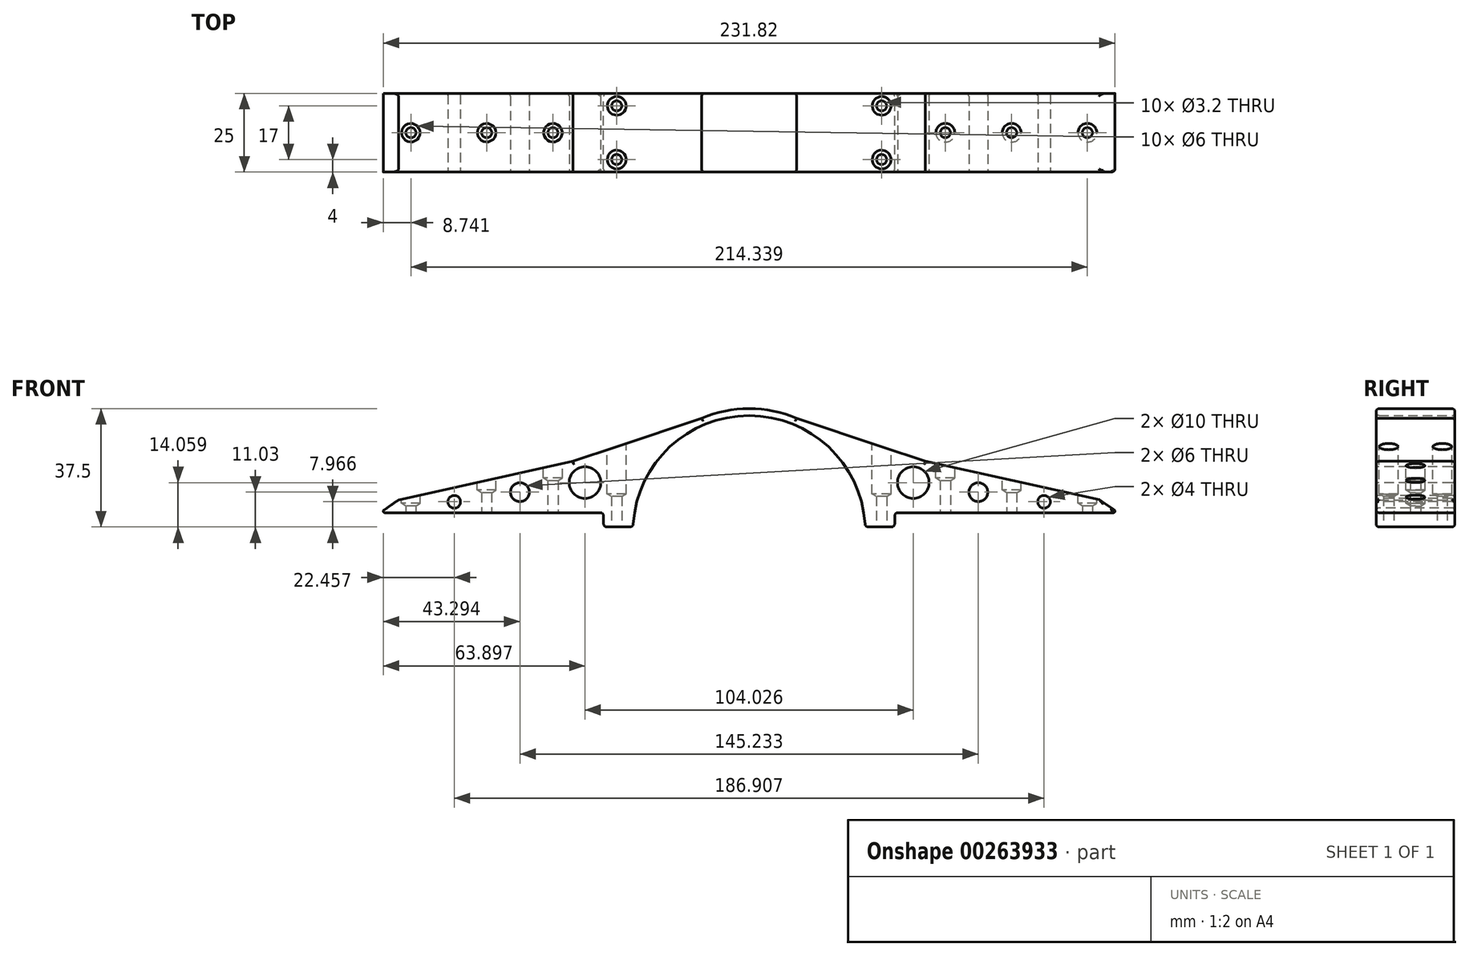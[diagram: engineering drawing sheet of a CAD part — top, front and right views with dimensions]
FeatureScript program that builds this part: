
annotation { "Feature Type Name" : "Feature", "Feature Type Description" : "" }
export const myFeature = defineFeature(function(context is Context, id is Id, definition is map)
    precondition{}
    {
        {
            var Q0;
            Q0=qCreatedBy(makeId("Front.planeOp"),FACE);
            var sketch = newSketch(context, id + "F0", { "sketchPlane" : qUnion([Q0])});
            skLineSegment(sketch, "E0", {"start": v(-117.03, 6) * mm, "end": v(-46.11, 6) * mm});
            skLineSegment(sketch, "E1", {"start": v(117.03, 6) * mm, "end": v(111.07, 10.06) * mm});
            skLineSegment(sketch, "E2", {"start": v(111.07, 10.06) * mm, "end": v(55.86, 22.32) * mm});
            skLineSegment(sketch, "E3", {"start": v(55.86, 22.32) * mm, "end": v(15, 36) * mm});
            skArc(sketch, "E4", {"start": v(15, 36) * mm, "mid": v(0, 39) * mm, "end": v(-15, 36) * mm});
            skPoint(sketch, "E5.start.orphan", {"position": v(39, 0) * mm});
            skLineSegment(sketch, "E6", {"start": v(36.71, 1.5) * mm, "end": v(46.11, 1.5) * mm});
            skLineSegment(sketch, "E7", {"start": v(46.11, 1.5) * mm, "end": v(46.11, 6) * mm});
            skLineSegment(sketch, "E8", {"start": v(15, 36) * mm, "end": v(15, 36) * mm});
            skArc(sketch, "E9", {"start": v(36.77, 1.5) * mm, "mid": v(0, 36.8) * mm, "end": v(-36.77, 1.5) * mm});
            skPoint(sketch, "E10.start.orphan", {"position": v(36.8, 0) * mm});
            skLineSegment(sketch, "E11", {"start": v(46.11, 6) * mm, "end": v(117.03, 6) * mm});
            skLineSegment(sketch, "E12.MirrorCS", {"start": v(-46.11, 1.5) * mm, "end": v(-46.11, 6) * mm});
            skLineSegment(sketch, "E13.MirrorCS", {"start": v(-36.71, 1.5) * mm, "end": v(-46.11, 1.5) * mm});
            skLineSegment(sketch, "E14.MirrorCS", {"start": v(-55.86, 22.32) * mm, "end": v(-15, 36) * mm});
            skLineSegment(sketch, "E15.MirrorCS", {"start": v(-111.07, 10.06) * mm, "end": v(-55.86, 22.32) * mm});
            skLineSegment(sketch, "E16.MirrorCS", {"start": v(-117.03, 6) * mm, "end": v(-111.07, 10.06) * mm});
            skSolve(sketch);
        }
        {
            var Q0;
            Q0 = qSketchRegion(id + "F0", true);
            extrude(context, id + "F1", {"entities" : qUnion([Q0]), "depth" : 25 * mm});
        }
        {
            var Q0;
            Q0=makeQuery(id+"F1.opExtrude","SWEPT_FACE",FACE,{"disambiguationData":[OSD([sQuery(id+"F0.wireOp",EDGE,"E6")])]});
            var sketch = newSketch(context, id + "F2", { "sketchPlane" : qUnion([Q0])});
            skLineSegment(sketch, "E17.0", {"start": v(36.77, 25) * mm, "end": v(36.77, 0) * mm});
            skPoint(sketch, "E18.0", {"position": v(41.44, 25) * mm});
            skLineSegment(sketch, "E19.0", {"start": v(46.11, 25) * mm, "end": v(46.11, 0) * mm});
            skPoint(sketch, "E20.0", {"position": v(41.44, 0) * mm});
            skLineSegment(sketch, "E21.0", {"start": v(36.77, 0) * mm, "end": v(46.11, 0) * mm});
            skLineSegment(sketch, "E22.0", {"start": v(36.77, 25) * mm, "end": v(46.11, 25) * mm});
            skLineSegment(sketch, "E23", {"start": v(41.97, 30.62) * mm, "end": v(41.97, -11.26) * mm, "construction": true});
            skCircle(sketch, "E24", {"center": v(41.97, 21) * mm, "radius": 1.75 * mm});
            skCircle(sketch, "E25", {"center": v(41.97, 4) * mm, "radius": 1.75 * mm});
            skCircle(sketch, "E26.MirrorC", {"center": v(-41.97, 21) * mm, "radius": 1.75 * mm});
            skCircle(sketch, "E27.MirrorC", {"center": v(-41.97, 4) * mm, "radius": 1.75 * mm});
            skSolve(sketch);
        }
        {
            var Q0;
            Q0=sQuery(id+"F2.wireOp",VERTEX,"E24.center");
            var Q1;
            Q1=sQuery(id+"F2.wireOp",VERTEX,"E25.center");
            var Q2;
            Q2=sQuery(id+"F2.wireOp",VERTEX,"E26.MirrorC.center");
            var Q3;
            Q3=sQuery(id+"F2.wireOp",VERTEX,"E27.MirrorC.center");
            var Q4;
            Q4=makeQuery(id+"F1.opExtrude","SWEPT_BODY",BODY,{"disambiguationData":[OSD([sQuery(id+"F0.wireOp",EDGE,"E0"),sQuery(id+"F0.wireOp",EDGE,"E1"),sQuery(id+"F0.wireOp",EDGE,"E2"),sQuery(id+"F0.wireOp",EDGE,"E3"),sQuery(id+"F0.wireOp",EDGE,"E4"),sQuery(id+"F0.wireOp",EDGE,"E6"),sQuery(id+"F0.wireOp",EDGE,"E7"),sQuery(id+"F0.wireOp",EDGE,"E9"),sQuery(id+"F0.wireOp",EDGE,"E11"),sQuery(id+"F0.wireOp",EDGE,"E12.MirrorCS"),sQuery(id+"F0.wireOp",EDGE,"E13.MirrorCS"),sQuery(id+"F0.wireOp",EDGE,"E14.MirrorCS"),sQuery(id+"F0.wireOp",EDGE,"E15.MirrorCS"),sQuery(id+"F0.wireOp",EDGE,"E16.MirrorCS")])]});
            hole(context, id + "F3", {"style" : HoleStyle.SIMPLE, "endStyle" : HoleEndStyle.THROUGH, "standardTappedOrClearance" : lookupTablePath({ "standard" : "ISO", "engagement" : "75%", "pitch" : "0.75 mm", "size" : "M4", "type" : "Tapped" }), "standardBlindInLast" : lookupTablePath({ "standard" : "ISO", "engagement" : "75%", "pitch" : "0.75 mm", "size" : "M4", "type" : "Tapped" }), "holeDiameter" : 3.2 * mm, "showTappedDepth" : true, "tappedDepth" : 12 * mm, "tapClearance" : 3, "locations" : qUnion([Q0, Q1, Q2, Q3]), "scope" : qUnion([Q4])});
        }
        {
            var Q0;
            Q0=makeQuery(id+"F1.opExtrude","SWEPT_FACE",FACE,{"disambiguationData":[OSD([sQuery(id+"F0.wireOp",EDGE,"E11")])]});
            var sketch = newSketch(context, id + "F4", { "sketchPlane" : qUnion([Q0])});
            skLineSegment(sketch, "E28.0", {"start": v(36.77, 25) * mm, "end": v(36.77, 0) * mm});
            skLineSegment(sketch, "E29.0", {"start": v(36.77, 25) * mm, "end": v(46.11, 25) * mm});
            skLineSegment(sketch, "E30.0", {"start": v(36.77, 0) * mm, "end": v(46.11, 0) * mm});
            skLineSegment(sketch, "E31.0", {"start": v(46.11, 25) * mm, "end": v(46.11, 0) * mm});
            skLineSegment(sketch, "E32.0", {"start": v(46.11, 25) * mm, "end": v(117.03, 25) * mm});
            skLineSegment(sketch, "E33.0", {"start": v(46.11, 0) * mm, "end": v(117.03, 0) * mm});
            skLineSegment(sketch, "E34", {"start": v(-152.17, 12.5) * mm, "end": v(189.53, 12.5) * mm, "construction": true});
            skLineSegment(sketch, "E35.0", {"start": v(-117.03, 25) * mm, "end": v(-46.11, 25) * mm});
            skLineSegment(sketch, "E36.0", {"start": v(-117.03, 0) * mm, "end": v(-46.11, 0) * mm});
            skCircle(sketch, "E37", {"center": v(62.17, 12.5) * mm, "radius": 1.5 * mm});
            skCircle(sketch, "E38", {"center": v(83.17, 12.5) * mm, "radius": 1.5 * mm});
            skCircle(sketch, "E39", {"center": v(107.17, 12.5) * mm, "radius": 1.5 * mm});
            skLineSegment(sketch, "E40", {"start": v(47.17, 31.58) * mm, "end": v(47.17, -3.17) * mm, "construction": true});
            skCircle(sketch, "E41.MirrorC", {"center": v(-62.17, 12.5) * mm, "radius": 1.5 * mm});
            skCircle(sketch, "E42.MirrorC", {"center": v(-83.17, 12.5) * mm, "radius": 1.5 * mm});
            skCircle(sketch, "E43.MirrorC", {"center": v(-107.17, 12.5) * mm, "radius": 1.5 * mm});
            skSolve(sketch);
        }
        {
            var Q0;
            Q0=sQuery(id+"F4.wireOp",VERTEX,"E39.center");
            var Q1;
            Q1=sQuery(id+"F4.wireOp",VERTEX,"E38.center");
            var Q2;
            Q2=sQuery(id+"F4.wireOp",VERTEX,"E37.center");
            var Q3;
            Q3=sQuery(id+"F4.wireOp",VERTEX,"E41.MirrorC.center");
            var Q4;
            Q4=sQuery(id+"F4.wireOp",VERTEX,"E42.MirrorC.center");
            var Q5;
            Q5=sQuery(id+"F4.wireOp",VERTEX,"E43.MirrorC.center");
            var Q6;
            Q6=makeQuery(id+"F1.opExtrude","SWEPT_BODY",BODY,{"disambiguationData":[OSD([sQuery(id+"F0.wireOp",EDGE,"E0"),sQuery(id+"F0.wireOp",EDGE,"E1"),sQuery(id+"F0.wireOp",EDGE,"E2"),sQuery(id+"F0.wireOp",EDGE,"E3"),sQuery(id+"F0.wireOp",EDGE,"E4"),sQuery(id+"F0.wireOp",EDGE,"E6"),sQuery(id+"F0.wireOp",EDGE,"E7"),sQuery(id+"F0.wireOp",EDGE,"E9"),sQuery(id+"F0.wireOp",EDGE,"E11"),sQuery(id+"F0.wireOp",EDGE,"E12.MirrorCS"),sQuery(id+"F0.wireOp",EDGE,"E13.MirrorCS"),sQuery(id+"F0.wireOp",EDGE,"E14.MirrorCS"),sQuery(id+"F0.wireOp",EDGE,"E15.MirrorCS"),sQuery(id+"F0.wireOp",EDGE,"E16.MirrorCS")])]});
            hole(context, id + "F5", {"style" : HoleStyle.SIMPLE, "endStyle" : HoleEndStyle.THROUGH, "standardTappedOrClearance" : lookupTablePath({ "standard" : "ISO", "engagement" : "75%", "pitch" : "0.75 mm", "size" : "M4", "type" : "Tapped" }), "standardBlindInLast" : lookupTablePath({ "standard" : "ISO", "engagement" : "75%", "pitch" : "0.75 mm", "size" : "M4", "type" : "Tapped" }), "holeDiameter" : 3.2 * mm, "showTappedDepth" : true, "tappedDepth" : 12 * mm, "tapClearance" : 3, "locations" : qUnion([Q0, Q1, Q2, Q3, Q4, Q5]), "scope" : qUnion([Q6])});
        }
        {
            var Q0;
            Q0=qCreatedBy(makeId("Top.planeOp"),FACE);
            cPlane(context, id + "F6", {"entities" : qUnion([Q0]), "cplaneType" : CPlaneType.OFFSET, "offset" : 28 * mm, "width" : 150 * mm, "height" : 150 * mm});
        }
        {
            var Q0;
            Q0=qCreatedBy(id+"F6.planeOp",FACE);
            var sketch = newSketch(context, id + "F7", { "sketchPlane" : qUnion([Q0])});
            skCircle(sketch, "E44.0", {"center": v(41.97, -4) * mm, "radius": 1.6 * mm, "construction": true});
            skCircle(sketch, "E45.0", {"center": v(41.97, -21) * mm, "radius": 1.6 * mm, "construction": true});
            skCircle(sketch, "E46.0", {"center": v(62.17, -12.5) * mm, "radius": 1.6 * mm});
            skCircle(sketch, "E47.0", {"center": v(83.17, -12.5) * mm, "radius": 1.6 * mm});
            skCircle(sketch, "E48.0", {"center": v(107.17, -12.5) * mm, "radius": 1.6 * mm});
            skCircle(sketch, "E49.0", {"center": v(-41.97, -4) * mm, "radius": 1.6 * mm, "construction": true});
            skCircle(sketch, "E50.0", {"center": v(-41.97, -21) * mm, "radius": 1.6 * mm, "construction": true});
            skCircle(sketch, "E51.0", {"center": v(-62.17, -12.5) * mm, "radius": 1.6 * mm});
            skCircle(sketch, "E52.0", {"center": v(-83.17, -12.5) * mm, "radius": 1.2 * mm});
            skCircle(sketch, "E53.0", {"center": v(-107.17, -12.5) * mm, "radius": 1.2 * mm});
            skCircle(sketch, "E54", {"center": v(41.97, -4) * mm, "radius": 2 * mm});
            skCircle(sketch, "E55", {"center": v(41.97, -21) * mm, "radius": 2 * mm});
            skCircle(sketch, "E56.MirrorC", {"center": v(-41.97, -4) * mm, "radius": 2 * mm});
            skCircle(sketch, "E57.MirrorC", {"center": v(-41.97, -21) * mm, "radius": 2 * mm});
            skSolve(sketch);
        }
        {
            var Q0;
            Q0=sQuery(id+"F7.wireOp",VERTEX,"E44.0.center");
            var Q1;
            Q1=sQuery(id+"F7.wireOp",VERTEX,"E45.0.center");
            var Q2;
            Q2=sQuery(id+"F7.wireOp",VERTEX,"E50.0.center");
            var Q3;
            Q3=sQuery(id+"F7.wireOp",VERTEX,"E49.0.center");
            var Q4;
            Q4=makeQuery(id+"F1.opExtrude","SWEPT_BODY",BODY,{"disambiguationData":[OSD([sQuery(id+"F0.wireOp",EDGE,"E0"),sQuery(id+"F0.wireOp",EDGE,"E1"),sQuery(id+"F0.wireOp",EDGE,"E2"),sQuery(id+"F0.wireOp",EDGE,"E3"),sQuery(id+"F0.wireOp",EDGE,"E4"),sQuery(id+"F0.wireOp",EDGE,"E6"),sQuery(id+"F0.wireOp",EDGE,"E7"),sQuery(id+"F0.wireOp",EDGE,"E9"),sQuery(id+"F0.wireOp",EDGE,"E11"),sQuery(id+"F0.wireOp",EDGE,"E12.MirrorCS"),sQuery(id+"F0.wireOp",EDGE,"E13.MirrorCS"),sQuery(id+"F0.wireOp",EDGE,"E14.MirrorCS"),sQuery(id+"F0.wireOp",EDGE,"E15.MirrorCS"),sQuery(id+"F0.wireOp",EDGE,"E16.MirrorCS")])]});
            hole(context, id + "F8", {"style" : HoleStyle.SIMPLE, "endStyle" : HoleEndStyle.BLIND, "holeDiameter" : 6 * mm, "holeDepth" : 16 * mm, "tappedDepth" : 12 * mm, "tapClearance" : 3, "startFromSketch" : true, "locations" : qUnion([Q0, Q1, Q2, Q3]), "scope" : qUnion([Q4])});
        }
        {
            var Q0;
            Q0=sQuery(id+"F7.wireOp",VERTEX,"E46.0.center");
            var Q1;
            Q1=sQuery(id+"F7.wireOp",VERTEX,"E51.0.center");
            var Q2;
            Q2=makeQuery(id+"F1.opExtrude","SWEPT_BODY",BODY,{"disambiguationData":[OSD([sQuery(id+"F0.wireOp",EDGE,"E0"),sQuery(id+"F0.wireOp",EDGE,"E1"),sQuery(id+"F0.wireOp",EDGE,"E2"),sQuery(id+"F0.wireOp",EDGE,"E3"),sQuery(id+"F0.wireOp",EDGE,"E4"),sQuery(id+"F0.wireOp",EDGE,"E6"),sQuery(id+"F0.wireOp",EDGE,"E7"),sQuery(id+"F0.wireOp",EDGE,"E9"),sQuery(id+"F0.wireOp",EDGE,"E11"),sQuery(id+"F0.wireOp",EDGE,"E12.MirrorCS"),sQuery(id+"F0.wireOp",EDGE,"E13.MirrorCS"),sQuery(id+"F0.wireOp",EDGE,"E14.MirrorCS"),sQuery(id+"F0.wireOp",EDGE,"E15.MirrorCS"),sQuery(id+"F0.wireOp",EDGE,"E16.MirrorCS")])]});
            hole(context, id + "F9", {"style" : HoleStyle.SIMPLE, "endStyle" : HoleEndStyle.BLIND, "holeDiameter" : 6 * mm, "holeDepth" : 11 * mm, "tappedDepth" : 8 * mm, "tapClearance" : 3, "startFromSketch" : true, "locations" : qUnion([Q0, Q1]), "scope" : qUnion([Q2])});
        }
        {
            var Q0;
            Q0=sQuery(id+"F7.wireOp",VERTEX,"E52.0.center");
            var Q1;
            Q1=sQuery(id+"F7.wireOp",VERTEX,"E47.0.center");
            var Q2;
            Q2=makeQuery(id+"F1.opExtrude","SWEPT_BODY",BODY,{"disambiguationData":[OSD([sQuery(id+"F0.wireOp",EDGE,"E0"),sQuery(id+"F0.wireOp",EDGE,"E1"),sQuery(id+"F0.wireOp",EDGE,"E2"),sQuery(id+"F0.wireOp",EDGE,"E3"),sQuery(id+"F0.wireOp",EDGE,"E4"),sQuery(id+"F0.wireOp",EDGE,"E6"),sQuery(id+"F0.wireOp",EDGE,"E7"),sQuery(id+"F0.wireOp",EDGE,"E9"),sQuery(id+"F0.wireOp",EDGE,"E11"),sQuery(id+"F0.wireOp",EDGE,"E12.MirrorCS"),sQuery(id+"F0.wireOp",EDGE,"E13.MirrorCS"),sQuery(id+"F0.wireOp",EDGE,"E14.MirrorCS"),sQuery(id+"F0.wireOp",EDGE,"E15.MirrorCS"),sQuery(id+"F0.wireOp",EDGE,"E16.MirrorCS")])]});
            hole(context, id + "F10", {"style" : HoleStyle.SIMPLE, "endStyle" : HoleEndStyle.BLIND, "holeDiameter" : 6 * mm, "holeDepth" : 14.85 * mm, "tappedDepth" : 11.1 * mm, "tapClearance" : 3, "startFromSketch" : true, "locations" : qUnion([Q0, Q1]), "scope" : qUnion([Q2])});
        }
        {
            var Q0;
            Q0=sQuery(id+"F7.wireOp",VERTEX,"E53.0.center");
            var Q1;
            Q1=sQuery(id+"F7.wireOp",VERTEX,"E48.0.center");
            var Q2;
            Q2=makeQuery(id+"F1.opExtrude","SWEPT_BODY",BODY,{"disambiguationData":[OSD([sQuery(id+"F0.wireOp",EDGE,"E0"),sQuery(id+"F0.wireOp",EDGE,"E1"),sQuery(id+"F0.wireOp",EDGE,"E2"),sQuery(id+"F0.wireOp",EDGE,"E3"),sQuery(id+"F0.wireOp",EDGE,"E4"),sQuery(id+"F0.wireOp",EDGE,"E6"),sQuery(id+"F0.wireOp",EDGE,"E7"),sQuery(id+"F0.wireOp",EDGE,"E9"),sQuery(id+"F0.wireOp",EDGE,"E11"),sQuery(id+"F0.wireOp",EDGE,"E12.MirrorCS"),sQuery(id+"F0.wireOp",EDGE,"E13.MirrorCS"),sQuery(id+"F0.wireOp",EDGE,"E14.MirrorCS"),sQuery(id+"F0.wireOp",EDGE,"E15.MirrorCS"),sQuery(id+"F0.wireOp",EDGE,"E16.MirrorCS")])]});
            hole(context, id + "F11", {"style" : HoleStyle.SIMPLE, "endStyle" : HoleEndStyle.BLIND, "holeDiameter" : 6 * mm, "holeDepth" : 19 * mm, "tappedDepth" : 16.1 * mm, "tapClearance" : 3, "startFromSketch" : true, "locations" : qUnion([Q0, Q1]), "scope" : qUnion([Q2])});
        }
        {
            var Q0;
            Q0=makeQuery(id+"F1.opExtrude","CAP_FACE",FACE,{"disambiguationData":[OSD([sQuery(id+"F0.wireOp",EDGE,"E0"),sQuery(id+"F0.wireOp",EDGE,"E1"),sQuery(id+"F0.wireOp",EDGE,"E2"),sQuery(id+"F0.wireOp",EDGE,"E3"),sQuery(id+"F0.wireOp",EDGE,"E4"),sQuery(id+"F0.wireOp",EDGE,"E6"),sQuery(id+"F0.wireOp",EDGE,"E7"),sQuery(id+"F0.wireOp",EDGE,"E9"),sQuery(id+"F0.wireOp",EDGE,"E11"),sQuery(id+"F0.wireOp",EDGE,"E12.MirrorCS"),sQuery(id+"F0.wireOp",EDGE,"E13.MirrorCS"),sQuery(id+"F0.wireOp",EDGE,"E14.MirrorCS"),sQuery(id+"F0.wireOp",EDGE,"E15.MirrorCS"),sQuery(id+"F0.wireOp",EDGE,"E16.MirrorCS")])],"isStart":false});
            var sketch = newSketch(context, id + "F12", { "sketchPlane" : qUnion([Q0])});
            skCircle(sketch, "E58", {"center": v(-52.01, 15.56) * mm, "radius": 5 * mm});
            skLineSegment(sketch, "E59", {"start": v(-62.12, 28.15) * mm, "end": v(-62.12, 0) * mm, "construction": true});
            skLineSegment(sketch, "E60", {"start": v(-41.91, 28) * mm, "end": v(-41.91, -0.66) * mm, "construction": true});
            skLineSegment(sketch, "E61", {"start": v(-83.2, 28.15) * mm, "end": v(-83.2, -0.74) * mm, "construction": true});
            skLineSegment(sketch, "E62", {"start": v(-83.31, -0.74) * mm, "end": v(-83.82, -0.74) * mm, "construction": true});
            skLineSegment(sketch, "E63", {"start": v(-107.05, 28) * mm, "end": v(-107.05, 0) * mm, "construction": true});
            skCircle(sketch, "E64", {"center": v(-72.62, 12.53) * mm, "radius": 3 * mm});
            skLineSegment(sketch, "E65", {"start": v(-117.03, 6) * mm, "end": v(-31.8, 18.53) * mm, "construction": true});
            skCircle(sketch, "E66", {"center": v(-93.45, 9.47) * mm, "radius": 2 * mm});
            skCircle(sketch, "E67.MirrorC", {"center": v(52.01, 15.56) * mm, "radius": 5 * mm});
            skCircle(sketch, "E68.MirrorC", {"center": v(72.62, 12.53) * mm, "radius": 3 * mm});
            skCircle(sketch, "E69.MirrorC", {"center": v(93.45, 9.47) * mm, "radius": 2 * mm});
            skSolve(sketch);
        }
        {
            var Q0;
            Q0 = qSketchRegion(id + "F12", true);
            extrude(context, id + "F13", {"entities" : qUnion([Q0]), "operationType" : NewBodyOperationType.REMOVE, "endBound" : BoundingType.THROUGH_ALL, "oppositeDirection" : true, "depth" : 25 * mm});
        }
        {
            var Q0;
            Q0=makeQuery(id+"F1.opExtrude","SWEPT_EDGE",EDGE,{"disambiguationData":[OSD([sQuery(id+"F0.wireOp",EDGE,"E9"),sQuery(id+"F0.wireOp",EDGE,"E13.MirrorCS")])]});
            var Q1;
            Q1=makeQuery(id+"F1.opExtrude","SWEPT_EDGE",EDGE,{"disambiguationData":[OSD([sQuery(id+"F0.wireOp",EDGE,"E6"),sQuery(id+"F0.wireOp",EDGE,"E9")])]});
            var Q2;
            Q2=makeQuery(id+"F1.opExtrude","SWEPT_EDGE",EDGE,{"disambiguationData":[OSD([sQuery(id+"F0.wireOp",EDGE,"E7"),sQuery(id+"F0.wireOp",EDGE,"E11")])]});
            var Q3;
            Q3=makeQuery(id+"F1.opExtrude","SWEPT_EDGE",EDGE,{"disambiguationData":[OSD([sQuery(id+"F0.wireOp",EDGE,"E6"),sQuery(id+"F0.wireOp",EDGE,"E7")])]});
            var Q4;
            Q4=makeQuery(id+"F1.opExtrude","SWEPT_EDGE",EDGE,{"disambiguationData":[OSD([sQuery(id+"F0.wireOp",EDGE,"E12.MirrorCS"),sQuery(id+"F0.wireOp",EDGE,"E13.MirrorCS")])]});
            var Q5;
            Q5=makeQuery(id+"F1.opExtrude","SWEPT_EDGE",EDGE,{"disambiguationData":[OSD([sQuery(id+"F0.wireOp",EDGE,"E0"),sQuery(id+"F0.wireOp",EDGE,"E12.MirrorCS")])]});
            var Q6;
            Q6=makeQuery(id+"F1.opExtrude","CAP_EDGE",EDGE,{"disambiguationData":[OSD([sQuery(id+"F0.wireOp",EDGE,"E12.MirrorCS")])],"isStart":true});
            var Q7;
            Q7=makeQuery(id+"F1.opExtrude","CAP_EDGE",EDGE,{"disambiguationData":[OSD([sQuery(id+"F0.wireOp",EDGE,"E13.MirrorCS")])],"isStart":true});
            var Q8;
            Q8=makeQuery(id+"F1.opExtrude","CAP_EDGE",EDGE,{"disambiguationData":[OSD([sQuery(id+"F0.wireOp",EDGE,"E6")])],"isStart":true});
            var Q9;
            Q9=makeQuery(id+"F1.opExtrude","CAP_EDGE",EDGE,{"disambiguationData":[OSD([sQuery(id+"F0.wireOp",EDGE,"E7")])],"isStart":true});
            var Q10;
            Q10=makeQuery(id+"F1.opExtrude","CAP_EDGE",EDGE,{"disambiguationData":[OSD([sQuery(id+"F0.wireOp",EDGE,"E12.MirrorCS")])],"isStart":false});
            var Q11;
            Q11=makeQuery(id+"F1.opExtrude","CAP_EDGE",EDGE,{"disambiguationData":[OSD([sQuery(id+"F0.wireOp",EDGE,"E13.MirrorCS")])],"isStart":false});
            var Q12;
            Q12=makeQuery(id+"F1.opExtrude","CAP_EDGE",EDGE,{"disambiguationData":[OSD([sQuery(id+"F0.wireOp",EDGE,"E6")])],"isStart":false});
            var Q13;
            Q13=makeQuery(id+"F1.opExtrude","CAP_EDGE",EDGE,{"disambiguationData":[OSD([sQuery(id+"F0.wireOp",EDGE,"E7")])],"isStart":false});
            var Q14;
            Q14=makeQuery(id+"F1.opExtrude","CAP_EDGE",EDGE,{"disambiguationData":[OSD([sQuery(id+"F0.wireOp",EDGE,"E11")])],"isStart":false});
            var Q15;
            Q15=makeQuery(id+"F1.opExtrude","CAP_EDGE",EDGE,{"disambiguationData":[OSD([sQuery(id+"F0.wireOp",EDGE,"E9")])],"isStart":false});
            var Q16;
            Q16=makeQuery(id+"F1.opExtrude","CAP_EDGE",EDGE,{"disambiguationData":[OSD([sQuery(id+"F0.wireOp",EDGE,"E9")])],"isStart":true});
            fillet(context, id + "F14", {"entities" : qUnion([Q0, Q1, Q2, Q3, Q4, Q5, Q6, Q7, Q8, Q9, Q10, Q11, Q12, Q13, Q14, Q15, Q16]), "radius" : 1 * mm, "tangentPropagation" : true, "allowEdgeOverflow" : false});
        }
        {
            var Q0;
            Q0=makeQuery(id+"F1.opExtrude","SWEPT_EDGE",EDGE,{"disambiguationData":[OSD([sQuery(id+"F0.wireOp",EDGE,"E0"),sQuery(id+"F0.wireOp",EDGE,"E16.MirrorCS")])]});
            var Q1;
            Q1=makeQuery(id+"F1.opExtrude","SWEPT_EDGE",EDGE,{"disambiguationData":[OSD([sQuery(id+"F0.wireOp",EDGE,"E1"),sQuery(id+"F0.wireOp",EDGE,"E11")])]});
            fillet(context, id + "F15", {"entities" : qUnion([Q0, Q1]), "radius" : .5 * mm, "tangentPropagation" : true, "allowEdgeOverflow" : false});
        }
        {
            var Q0;
            Q0=makeQuery(id+"F1.opExtrude","CAP_EDGE",EDGE,{"disambiguationData":[OSD([sQuery(id+"F0.wireOp",EDGE,"E15.MirrorCS")])],"isStart":false});
            var Q1;
            Q1=makeQuery(id+"F1.opExtrude","CAP_EDGE",EDGE,{"disambiguationData":[OSD([sQuery(id+"F0.wireOp",EDGE,"E14.MirrorCS")])],"isStart":false});
            var Q2;
            Q2=makeQuery(id+"F1.opExtrude","CAP_EDGE",EDGE,{"disambiguationData":[OSD([sQuery(id+"F0.wireOp",EDGE,"E4")])],"isStart":false});
            var Q3;
            Q3=makeQuery(id+"F1.opExtrude","CAP_EDGE",EDGE,{"disambiguationData":[OSD([sQuery(id+"F0.wireOp",EDGE,"E3")])],"isStart":false});
            var Q4;
            Q4=makeQuery(id+"F1.opExtrude","CAP_EDGE",EDGE,{"disambiguationData":[OSD([sQuery(id+"F0.wireOp",EDGE,"E2")])],"isStart":false});
            var Q5;
            Q5=makeQuery(id+"F1.opExtrude","CAP_EDGE",EDGE,{"disambiguationData":[OSD([sQuery(id+"F0.wireOp",EDGE,"E2")])],"isStart":true});
            var Q6;
            Q6=makeQuery(id+"F1.opExtrude","CAP_EDGE",EDGE,{"disambiguationData":[OSD([sQuery(id+"F0.wireOp",EDGE,"E3")])],"isStart":true});
            var Q7;
            Q7=makeQuery(id+"F1.opExtrude","CAP_EDGE",EDGE,{"disambiguationData":[OSD([sQuery(id+"F0.wireOp",EDGE,"E4")])],"isStart":true});
            var Q8;
            Q8=makeQuery(id+"F1.opExtrude","CAP_EDGE",EDGE,{"disambiguationData":[OSD([sQuery(id+"F0.wireOp",EDGE,"E14.MirrorCS")])],"isStart":true});
            var Q9;
            Q9=makeQuery(id+"F1.opExtrude","CAP_EDGE",EDGE,{"disambiguationData":[OSD([sQuery(id+"F0.wireOp",EDGE,"E15.MirrorCS")])],"isStart":true});
            var Q10;
            Q10=makeQuery(id+"F13.boolean.opBoolean","COPY",EDGE,{"derivedFrom":makeQuery(id+"F13.opExtrude","CAP_EDGE",EDGE,{"disambiguationData":[OSD([sQuery(id+"F12.wireOp",EDGE,"E64")])],"isStart":true})});
            var Q11;
            Q11=makeQuery(id+"F13.boolean.opBoolean","COPY",EDGE,{"derivedFrom":makeQuery(id+"F13.opExtrude","CAP_EDGE",EDGE,{"disambiguationData":[OSD([sQuery(id+"F12.wireOp",EDGE,"E58")])],"isStart":true})});
            var Q12;
            Q12=makeQuery(id+"F13.boolean.opBoolean","COPY",EDGE,{"derivedFrom":makeQuery(id+"F13.opExtrude","CAP_EDGE",EDGE,{"disambiguationData":[OSD([sQuery(id+"F12.wireOp",EDGE,"E67.MirrorC")])],"isStart":true})});
            var Q13;
            Q13=makeQuery(id+"F13.boolean.opBoolean","COPY",EDGE,{"derivedFrom":makeQuery(id+"F13.opExtrude","CAP_EDGE",EDGE,{"disambiguationData":[OSD([sQuery(id+"F12.wireOp",EDGE,"E68.MirrorC")])],"isStart":true})});
            var Q14;
            Q14=makeQuery(id+"F13.boolean.opBoolean","INTERSECT",EDGE,{"derivedFrom":[makeQuery(id+"F1.opExtrude","CAP_FACE",FACE,{"disambiguationData":[OSD([sQuery(id+"F0.wireOp",EDGE,"E0"),sQuery(id+"F0.wireOp",EDGE,"E1"),sQuery(id+"F0.wireOp",EDGE,"E2"),sQuery(id+"F0.wireOp",EDGE,"E3"),sQuery(id+"F0.wireOp",EDGE,"E4"),sQuery(id+"F0.wireOp",EDGE,"E6"),sQuery(id+"F0.wireOp",EDGE,"E7"),sQuery(id+"F0.wireOp",EDGE,"E9"),sQuery(id+"F0.wireOp",EDGE,"E11"),sQuery(id+"F0.wireOp",EDGE,"E12.MirrorCS"),sQuery(id+"F0.wireOp",EDGE,"E13.MirrorCS"),sQuery(id+"F0.wireOp",EDGE,"E14.MirrorCS"),sQuery(id+"F0.wireOp",EDGE,"E15.MirrorCS"),sQuery(id+"F0.wireOp",EDGE,"E16.MirrorCS")])],"isStart":true}),makeQuery(id+"F13.opExtrude","SWEPT_FACE",FACE,{"disambiguationData":[OSD([sQuery(id+"F12.wireOp",EDGE,"E64")])]})]});
            var Q15;
            Q15=makeQuery(id+"F13.boolean.opBoolean","INTERSECT",EDGE,{"derivedFrom":[makeQuery(id+"F1.opExtrude","CAP_FACE",FACE,{"disambiguationData":[OSD([sQuery(id+"F0.wireOp",EDGE,"E0"),sQuery(id+"F0.wireOp",EDGE,"E1"),sQuery(id+"F0.wireOp",EDGE,"E2"),sQuery(id+"F0.wireOp",EDGE,"E3"),sQuery(id+"F0.wireOp",EDGE,"E4"),sQuery(id+"F0.wireOp",EDGE,"E6"),sQuery(id+"F0.wireOp",EDGE,"E7"),sQuery(id+"F0.wireOp",EDGE,"E9"),sQuery(id+"F0.wireOp",EDGE,"E11"),sQuery(id+"F0.wireOp",EDGE,"E12.MirrorCS"),sQuery(id+"F0.wireOp",EDGE,"E13.MirrorCS"),sQuery(id+"F0.wireOp",EDGE,"E14.MirrorCS"),sQuery(id+"F0.wireOp",EDGE,"E15.MirrorCS"),sQuery(id+"F0.wireOp",EDGE,"E16.MirrorCS")])],"isStart":true}),makeQuery(id+"F13.opExtrude","SWEPT_FACE",FACE,{"disambiguationData":[OSD([sQuery(id+"F12.wireOp",EDGE,"E58")])]})]});
            var Q16;
            Q16=makeQuery(id+"F13.boolean.opBoolean","INTERSECT",EDGE,{"derivedFrom":[makeQuery(id+"F1.opExtrude","CAP_FACE",FACE,{"disambiguationData":[OSD([sQuery(id+"F0.wireOp",EDGE,"E0"),sQuery(id+"F0.wireOp",EDGE,"E1"),sQuery(id+"F0.wireOp",EDGE,"E2"),sQuery(id+"F0.wireOp",EDGE,"E3"),sQuery(id+"F0.wireOp",EDGE,"E4"),sQuery(id+"F0.wireOp",EDGE,"E6"),sQuery(id+"F0.wireOp",EDGE,"E7"),sQuery(id+"F0.wireOp",EDGE,"E9"),sQuery(id+"F0.wireOp",EDGE,"E11"),sQuery(id+"F0.wireOp",EDGE,"E12.MirrorCS"),sQuery(id+"F0.wireOp",EDGE,"E13.MirrorCS"),sQuery(id+"F0.wireOp",EDGE,"E14.MirrorCS"),sQuery(id+"F0.wireOp",EDGE,"E15.MirrorCS"),sQuery(id+"F0.wireOp",EDGE,"E16.MirrorCS")])],"isStart":true}),makeQuery(id+"F13.opExtrude","SWEPT_FACE",FACE,{"disambiguationData":[OSD([sQuery(id+"F12.wireOp",EDGE,"E67.MirrorC")])]})]});
            var Q17;
            Q17=makeQuery(id+"F13.boolean.opBoolean","INTERSECT",EDGE,{"derivedFrom":[makeQuery(id+"F1.opExtrude","CAP_FACE",FACE,{"disambiguationData":[OSD([sQuery(id+"F0.wireOp",EDGE,"E0"),sQuery(id+"F0.wireOp",EDGE,"E1"),sQuery(id+"F0.wireOp",EDGE,"E2"),sQuery(id+"F0.wireOp",EDGE,"E3"),sQuery(id+"F0.wireOp",EDGE,"E4"),sQuery(id+"F0.wireOp",EDGE,"E6"),sQuery(id+"F0.wireOp",EDGE,"E7"),sQuery(id+"F0.wireOp",EDGE,"E9"),sQuery(id+"F0.wireOp",EDGE,"E11"),sQuery(id+"F0.wireOp",EDGE,"E12.MirrorCS"),sQuery(id+"F0.wireOp",EDGE,"E13.MirrorCS"),sQuery(id+"F0.wireOp",EDGE,"E14.MirrorCS"),sQuery(id+"F0.wireOp",EDGE,"E15.MirrorCS"),sQuery(id+"F0.wireOp",EDGE,"E16.MirrorCS")])],"isStart":true}),makeQuery(id+"F13.opExtrude","SWEPT_FACE",FACE,{"disambiguationData":[OSD([sQuery(id+"F12.wireOp",EDGE,"E68.MirrorC")])]})]});
            fillet(context, id + "F16", {"entities" : qUnion([Q0, Q1, Q2, Q3, Q4, Q5, Q6, Q7, Q8, Q9, Q10, Q11, Q12, Q13, Q14, Q15, Q16, Q17]), "radius" : 1 * mm, "tangentPropagation" : true, "allowEdgeOverflow" : false});
        }
        {
            var Q0;
            Q0=makeQuery(id+"F13.boolean.opBoolean","INTERSECT",EDGE,{"derivedFrom":[makeQuery(id+"F1.opExtrude","CAP_FACE",FACE,{"disambiguationData":[OSD([sQuery(id+"F0.wireOp",EDGE,"E0"),sQuery(id+"F0.wireOp",EDGE,"E1"),sQuery(id+"F0.wireOp",EDGE,"E2"),sQuery(id+"F0.wireOp",EDGE,"E3"),sQuery(id+"F0.wireOp",EDGE,"E4"),sQuery(id+"F0.wireOp",EDGE,"E6"),sQuery(id+"F0.wireOp",EDGE,"E7"),sQuery(id+"F0.wireOp",EDGE,"E9"),sQuery(id+"F0.wireOp",EDGE,"E11"),sQuery(id+"F0.wireOp",EDGE,"E12.MirrorCS"),sQuery(id+"F0.wireOp",EDGE,"E13.MirrorCS"),sQuery(id+"F0.wireOp",EDGE,"E14.MirrorCS"),sQuery(id+"F0.wireOp",EDGE,"E15.MirrorCS"),sQuery(id+"F0.wireOp",EDGE,"E16.MirrorCS")])],"isStart":true}),makeQuery(id+"F13.opExtrude","SWEPT_FACE",FACE,{"disambiguationData":[OSD([sQuery(id+"F12.wireOp",EDGE,"E66")])]})]});
            var Q1;
            Q1=makeQuery(id+"F13.boolean.opBoolean","INTERSECT",EDGE,{"derivedFrom":[makeQuery(id+"F1.opExtrude","CAP_FACE",FACE,{"disambiguationData":[OSD([sQuery(id+"F0.wireOp",EDGE,"E0"),sQuery(id+"F0.wireOp",EDGE,"E1"),sQuery(id+"F0.wireOp",EDGE,"E2"),sQuery(id+"F0.wireOp",EDGE,"E3"),sQuery(id+"F0.wireOp",EDGE,"E4"),sQuery(id+"F0.wireOp",EDGE,"E6"),sQuery(id+"F0.wireOp",EDGE,"E7"),sQuery(id+"F0.wireOp",EDGE,"E9"),sQuery(id+"F0.wireOp",EDGE,"E11"),sQuery(id+"F0.wireOp",EDGE,"E12.MirrorCS"),sQuery(id+"F0.wireOp",EDGE,"E13.MirrorCS"),sQuery(id+"F0.wireOp",EDGE,"E14.MirrorCS"),sQuery(id+"F0.wireOp",EDGE,"E15.MirrorCS"),sQuery(id+"F0.wireOp",EDGE,"E16.MirrorCS")])],"isStart":true}),makeQuery(id+"F13.opExtrude","SWEPT_FACE",FACE,{"disambiguationData":[OSD([sQuery(id+"F12.wireOp",EDGE,"E69.MirrorC")])]})]});
            var Q2;
            Q2=makeQuery(id+"F13.boolean.opBoolean","COPY",EDGE,{"derivedFrom":makeQuery(id+"F13.opExtrude","CAP_EDGE",EDGE,{"disambiguationData":[OSD([sQuery(id+"F12.wireOp",EDGE,"E66")])],"isStart":true})});
            var Q3;
            Q3=makeQuery(id+"F13.boolean.opBoolean","COPY",EDGE,{"derivedFrom":makeQuery(id+"F13.opExtrude","CAP_EDGE",EDGE,{"disambiguationData":[OSD([sQuery(id+"F12.wireOp",EDGE,"E69.MirrorC")])],"isStart":true})});
            fillet(context, id + "F17", {"entities" : qUnion([Q0, Q1, Q2, Q3]), "radius" : .5 * mm, "tangentPropagation" : true, "allowEdgeOverflow" : false});
        }
    });
